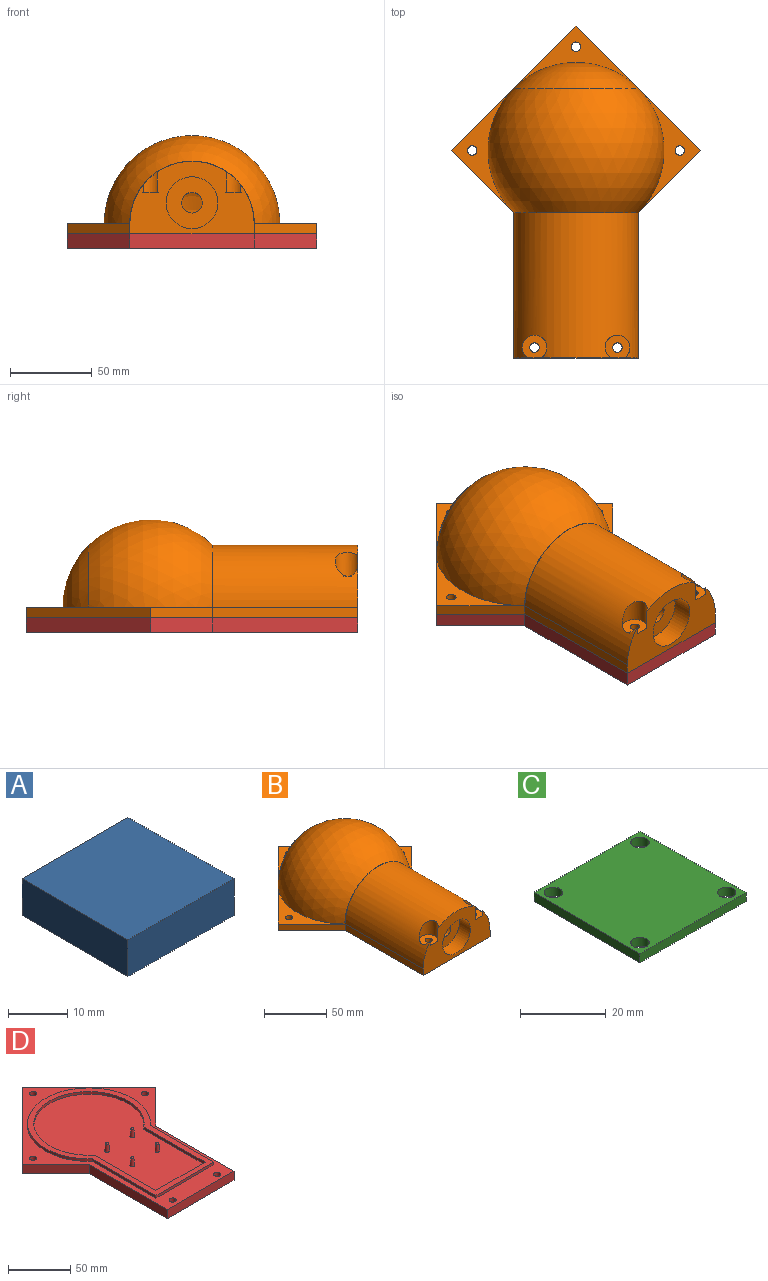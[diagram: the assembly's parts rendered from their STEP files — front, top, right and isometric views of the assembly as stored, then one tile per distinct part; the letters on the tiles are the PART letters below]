
ASSEMBLY  parts=4 mates=3
PART A: 6 faces, bbox 25.4x25.4x7.6 mm
  f0: plane 25.4x7.62mm, normal (0,1,0), area 193.5mm2, adj f1,f3,f4,f5
  f1: plane 25.4x7.62mm, normal (-1,0,0), area 193.5mm2, adj f0,f2,f4,f5
  f2: plane 25.4x7.62mm, normal (0,-1,0), area 193.5mm2, adj f1,f3,f4,f5
  f3: plane 25.4x7.62mm, normal (1,0,0), area 193.5mm2, adj f0,f2,f4,f5
  f4: plane 25.4x25.4mm, normal (0,0,1), area 645.2mm2, adj f0,f1,f2,f3
  f5: plane 25.4x25.4mm, normal (0,0,-1), area 645.2mm2, adj f0,f1,f2,f3
PART B: 36 faces, bbox 152.7x203.5x60.3 mm
  f0: cylinder r=6.35mm len=12.7mm, axis (0,-1,0), area 202.7mm2, adj f12,f35
  f1: cylinder r=38.1mm len=88.9mm, axis (0,-1,0), area 10153.5mm2, adj f5,f6,f7,f18,f28,f29,f30,f31
  f2: plane 76.2x38.1mm, normal (0,0,1), area 598.8mm2, adj f8,f9,f19,f25
  f3: plane 76.2x38.1mm, normal (0,0,1), area 598.8mm2, adj f9,f14,f17,f24
  f4: plane 38.23x38.23mm, normal (-0.71,-0.71,0), area 343.3mm2, adj f5,f14,f15,f16,f18
  f5: plane 88.9x6.35mm, normal (-1,0,0), area 564.5mm2, adj f1,f4,f6,f16
  f6: plane 76.2x44.45mm, normal (0,-1,0), area 1818mm2, adj f1,f5,f7,f16,f28,f29,f30,f31
  f7: plane 88.9x6.35mm, normal (1,0,0), area 564.5mm2, adj f1,f6,f8,f16
  f8: plane 38.23x38.23mm, normal (0.71,-0.71,0), area 343.3mm2, adj f2,f7,f9,f16,f18
  f9: plane 76.33x76.33mm, normal (0.71,0.71,0), area 685.5mm2, adj f2,f3,f8,f14,f16,f20
  f10: cylinder r=49.53mm len=99.06mm, axis (0,0,-1), area 1517.1mm2, adj f11,f13,f16,f22
  f11: plane 72.43x6.35mm, normal (-1,0,0), area 460mm2, adj f10,f12,f16,f21
  f12: plane 66.04x39.37mm, normal (0,1,0), area 2005.3mm2, adj f0,f11,f13,f16,f21
  f13: plane 72.43x6.35mm, normal (1,0,0), area 460mm2, adj f10,f12,f16,f21
  f14: plane 76.33x76.33mm, normal (-0.71,0.71,0), area 685.5mm2, adj f3,f4,f9,f15,f16,f20
  f15: plane 76.2x38.1mm, normal (0,0,1), area 598.8mm2, adj f4,f14,f19,f23
  f16: plane 203.46x152.66mm, normal (0,0,-1), area 4924.2mm2, adj f4,f5,f6,f7,f8,f9,f10,f11
  f17: sphere r=53.98mm, area 2669.5mm2, adj f3,f20
  f18: cone r=38.1mm half-angle=45deg, axis (0,1,0), area 22.4mm2, adj f1,f4,f8,f19
  f19: sphere r=53.98mm, area 12921.1mm2, adj f2,f15,f18,f20
  f20: cone r=38.1mm half-angle=45deg, axis (0,-1,0), area 22.4mm2, adj f9,f14,f17,f19
  f21: cylinder r=33.02mm len=72.43mm, axis (0,-1,0), area 7514mm2, adj f11,f12,f13,f22
  f22: sphere r=49.53mm, area 13451.5mm2, adj f10,f21
  f23: cylinder r=2.9mm len=6.35mm, axis (0,0,1), area 115.7mm2, adj f15,f16
  f24: cylinder r=2.9mm len=6.35mm, axis (0,0,1), area 115.7mm2, adj f3,f16
  f25: cylinder r=2.9mm len=6.35mm, axis (0,0,1), area 115.7mm2, adj f2,f16
  f26: cylinder r=2.9mm len=25.4mm, axis (0,0,-1), area 462.8mm2, adj f16,f33
  f27: cylinder r=2.9mm len=25.4mm, axis (0,0,-1), area 462.8mm2, adj f16,f30
  f28: cylinder r=7.62mm len=15.22mm, axis (0,0,-1), area 305mm2, adj f1,f6,f30
  f29: cylinder r=7.62mm len=5.74mm, axis (0,0,-1), area 13.4mm2, adj f1,f6,f30
  f30: plane 15.22x13.97mm, normal (0,0,1), area 148.7mm2, adj f1,f6,f27,f28,f29
  f31: cylinder r=7.62mm len=5.74mm, axis (0,0,-1), area 13.4mm2, adj f1,f6,f33
  f32: cylinder r=7.62mm len=15.22mm, axis (0,0,-1), area 304.9mm2, adj f1,f6,f33
  f33: plane 15.22x13.97mm, normal (0,0,1), area 148.7mm2, adj f1,f6,f26,f31,f32
  f34: cylinder r=15.88mm len=31.75mm, axis (0,-1,0), area 1266.8mm2, adj f6,f35
  f35: plane 31.75x31.75mm, normal (0,-1,0), area 665.1mm2, adj f0,f34
PART C: 10 faces, bbox 34.9x34.9x2.5 mm
  f0: plane 34.93x2.54mm, normal (1,0,0), area 88.7mm2, adj f1,f3,f4,f5
  f1: plane 34.93x2.54mm, normal (0,1,0), area 88.7mm2, adj f0,f2,f4,f5
  f2: plane 34.93x2.54mm, normal (-1,0,0), area 88.7mm2, adj f1,f3,f4,f5
  f3: plane 34.93x2.54mm, normal (0,-1,0), area 88.7mm2, adj f0,f2,f4,f5
  f4: plane 34.93x34.93mm, normal (0,0,1), area 1161.7mm2, adj f0,f1,f2,f3,f6,f7,f8,f9
  f5: plane 34.93x34.93mm, normal (0,0,-1), area 1161.7mm2, adj f0,f1,f2,f3,f6,f7,f8,f9
  f6: cylinder r=2.15mm len=4.3mm, axis (0,0,1), area 34.3mm2, adj f4,f5
  f7: cylinder r=2.15mm len=4.3mm, axis (0,0,1), area 34.3mm2, adj f4,f5
  f8: cylinder r=2.15mm len=4.3mm, axis (0,0,1), area 34.3mm2, adj f4,f5
  f9: cylinder r=2.15mm len=4.3mm, axis (0,0,1), area 34.3mm2, adj f4,f5
PART D: 67 faces, bbox 152.7x203.5x16.5 mm
  f0: cone r=1.91mm half-angle=4.8deg, axis (0,0,-1), area 76.3mm2, adj f1,f24
  f1: plane 2.54x2.54mm, normal (0,0,1), area 5.1mm2, adj f0
  f2: cone r=1.91mm half-angle=4.8deg, axis (0,0,-1), area 76.3mm2, adj f3,f24
  f3: plane 2.54x2.54mm, normal (0,0,1), area 5.1mm2, adj f2
  f4: cone r=1.91mm half-angle=4.8deg, axis (0,0,-1), area 76.3mm2, adj f5,f24
  f5: plane 2.54x2.54mm, normal (0,0,1), area 5.1mm2, adj f4
  f6: plane 38.23x38.23mm, normal (-0.71,-0.71,0), area 480.7mm2, adj f7,f12,f13,f14
  f7: plane 88.9x8.89mm, normal (-1,0,0), area 790.3mm2, adj f6,f8,f13,f14
  f8: plane 76.2x8.89mm, normal (0,-1,0), area 677.4mm2, adj f7,f9,f13,f14
  f9: plane 88.9x8.89mm, normal (1,0,0), area 790.3mm2, adj f8,f10,f13,f14
  f10: plane 38.23x38.23mm, normal (0.71,-0.71,0), area 480.7mm2, adj f9,f11,f13,f14
  f11: plane 76.33x76.33mm, normal (0.71,0.71,0), area 959.7mm2, adj f10,f12,f13,f14
  f12: plane 76.33x76.33mm, normal (-0.71,0.71,0), area 959.7mm2, adj f6,f11,f13,f14
  f13: plane 203.46x152.66mm, normal (0,0,1), area 4924.2mm2, adj f6,f7,f8,f9,f10,f11,f12,f15
  f14: plane 203.46x152.66mm, normal (0,0,-1), area 16698.6mm2, adj f6,f7,f8,f9,f10,f11,f12,f25
  f15: cylinder r=49.53mm len=99.06mm, axis (0,0,-1), area 606.9mm2, adj f13,f16,f22,f23
  f16: plane 72.43x2.54mm, normal (-1,0,0), area 184mm2, adj f13,f15,f17,f23
  f17: plane 66.04x2.54mm, normal (0,-1,0), area 167.7mm2, adj f13,f16,f22,f23
  f18: plane 69.7x2.54mm, normal (1,0,0), area 177mm2, adj f19,f21,f23,f24
  f19: cylinder r=44.45mm len=88.9mm, axis (0,0,-1), area 555.9mm2, adj f18,f20,f23,f24
  f20: plane 69.7x2.54mm, normal (-1,0,0), area 177mm2, adj f19,f21,f23,f24
  f21: plane 55.88x2.54mm, normal (0,1,0), area 141.9mm2, adj f18,f20,f23,f24
  f22: plane 72.43x2.54mm, normal (1,0,0), area 184mm2, adj f13,f15,f17,f23
  f23: plane 158.88x99.06mm, normal (0,0,1), area 2194.4mm2, adj f15,f16,f17,f18,f19,f20,f21,f22
  f24: plane 148.72x88.9mm, normal (0,0,1), area 9679.4mm2, adj f0,f2,f4,f18,f19,f20,f21,f65
  f25: plane 4x3.99mm, normal (0.87,-0.5,0), area 18.4mm2, adj f14,f26,f30,f31
  f26: plane 4.62x3.99mm, normal (0,-1,0), area 18.4mm2, adj f14,f25,f27,f31
  f27: plane 4x3.99mm, normal (-0.87,-0.5,0), area 18.4mm2, adj f14,f26,f28,f31
  f28: plane 4x3.99mm, normal (-0.87,0.5,0), area 18.4mm2, adj f14,f27,f29,f31
  f29: plane 4.62x3.99mm, normal (0,1,0), area 18.4mm2, adj f14,f28,f30,f31
  f30: plane 4x3.99mm, normal (0.87,0.5,0), area 18.4mm2, adj f14,f25,f29,f31
  f31: plane 9.24x8mm, normal (0,0,-1), area 29mm2, adj f25,f26,f27,f28,f29,f30,f64
  f32: plane 4x3.99mm, normal (0.87,-0.5,0), area 18.4mm2, adj f14,f33,f37,f38
  f33: plane 4.62x3.99mm, normal (0,-1,0), area 18.4mm2, adj f14,f32,f34,f38
  f34: plane 4x3.99mm, normal (-0.87,-0.5,0), area 18.4mm2, adj f14,f33,f35,f38
  f35: plane 4x3.99mm, normal (-0.87,0.5,0), area 18.4mm2, adj f14,f34,f36,f38
  f36: plane 4.62x3.99mm, normal (0,1,0), area 18.4mm2, adj f14,f35,f37,f38
  f37: plane 4x3.99mm, normal (0.87,0.5,0), area 18.4mm2, adj f14,f32,f36,f38
  f38: plane 9.24x8mm, normal (0,0,-1), area 29mm2, adj f32,f33,f34,f35,f36,f37,f63
  f39: plane 4x3.99mm, normal (0.87,-0.5,0), area 18.4mm2, adj f14,f40,f44,f45
  f40: plane 4.62x3.99mm, normal (0,-1,0), area 18.4mm2, adj f14,f39,f41,f45
  f41: plane 4x3.99mm, normal (-0.87,-0.5,0), area 18.4mm2, adj f14,f40,f42,f45
  f42: plane 4x3.99mm, normal (-0.87,0.5,0), area 18.4mm2, adj f14,f41,f43,f45
  f43: plane 4.62x3.99mm, normal (0,1,0), area 18.4mm2, adj f14,f42,f44,f45
  f44: plane 4x3.99mm, normal (0.87,0.5,0), area 18.4mm2, adj f14,f39,f43,f45
  f45: plane 9.24x8mm, normal (0,0,-1), area 29mm2, adj f39,f40,f41,f42,f43,f44,f62
  f46: plane 4x3.99mm, normal (0.87,-0.5,0), area 18.4mm2, adj f14,f47,f51,f52
  f47: plane 4.62x3.99mm, normal (0,-1,0), area 18.4mm2, adj f14,f46,f48,f52
  f48: plane 4x3.99mm, normal (-0.87,-0.5,0), area 18.4mm2, adj f14,f47,f49,f52
  f49: plane 4x3.99mm, normal (-0.87,0.5,0), area 18.4mm2, adj f14,f48,f50,f52
  f50: plane 4.62x3.99mm, normal (0,1,0), area 18.4mm2, adj f14,f49,f51,f52
  f51: plane 4x3.99mm, normal (0.87,0.5,0), area 18.4mm2, adj f14,f46,f50,f52
  f52: plane 9.24x8mm, normal (0,0,-1), area 29mm2, adj f46,f47,f48,f49,f50,f51,f61
  f53: plane 4x3.99mm, normal (0.87,-0.5,0), area 18.4mm2, adj f14,f54,f58,f59
  f54: plane 4.62x3.99mm, normal (0,-1,0), area 18.4mm2, adj f14,f53,f55,f59
  f55: plane 4x3.99mm, normal (-0.87,-0.5,0), area 18.4mm2, adj f14,f54,f56,f59
  f56: plane 4x3.99mm, normal (-0.87,0.5,0), area 18.4mm2, adj f14,f55,f57,f59
  f57: plane 4.62x3.99mm, normal (0,1,0), area 18.4mm2, adj f14,f56,f58,f59
  f58: plane 4x3.99mm, normal (0.87,0.5,0), area 18.4mm2, adj f14,f53,f57,f59
  f59: plane 9.24x8mm, normal (0,0,-1), area 29mm2, adj f53,f54,f55,f56,f57,f58,f60
  f60: cylinder r=2.9mm len=5.8mm, axis (0,0,-1), area 89.3mm2, adj f13,f59
  f61: cylinder r=2.9mm len=5.8mm, axis (0,0,-1), area 89.3mm2, adj f13,f52
  f62: cylinder r=2.9mm len=5.8mm, axis (0,0,-1), area 89.3mm2, adj f13,f45
  f63: cylinder r=2.9mm len=5.8mm, axis (0,0,-1), area 89.3mm2, adj f13,f38
  f64: cylinder r=2.9mm len=5.8mm, axis (0,0,-1), area 89.3mm2, adj f13,f31
  f65: cone r=1.91mm half-angle=4.8deg, axis (0,0,-1), area 76.3mm2, adj f24,f66
  f66: plane 2.54x2.54mm, normal (0,0,1), area 5.1mm2, adj f65
PLACE A t=(-68.08,-24.21,7.22)mm
PLACE B t=(-166.12,20.38,-38.25)mm
PLACE C t=(0,-28.96,11.03)mm
PLACE D t=(0,20.38,-1.67)mm
MATE fastened C.f9 <-> D.f2  axis (0,0,-1) through (14.28,-14.67,11.03)mm
MATE fastened B.f24 <-> D.f61  axis (0,0,-1) through (0,84.01,7.22)mm
MATE fastened A.f5 <-> D.f19  axis (0,0,-1) through (0,20.38,7.22)mm
